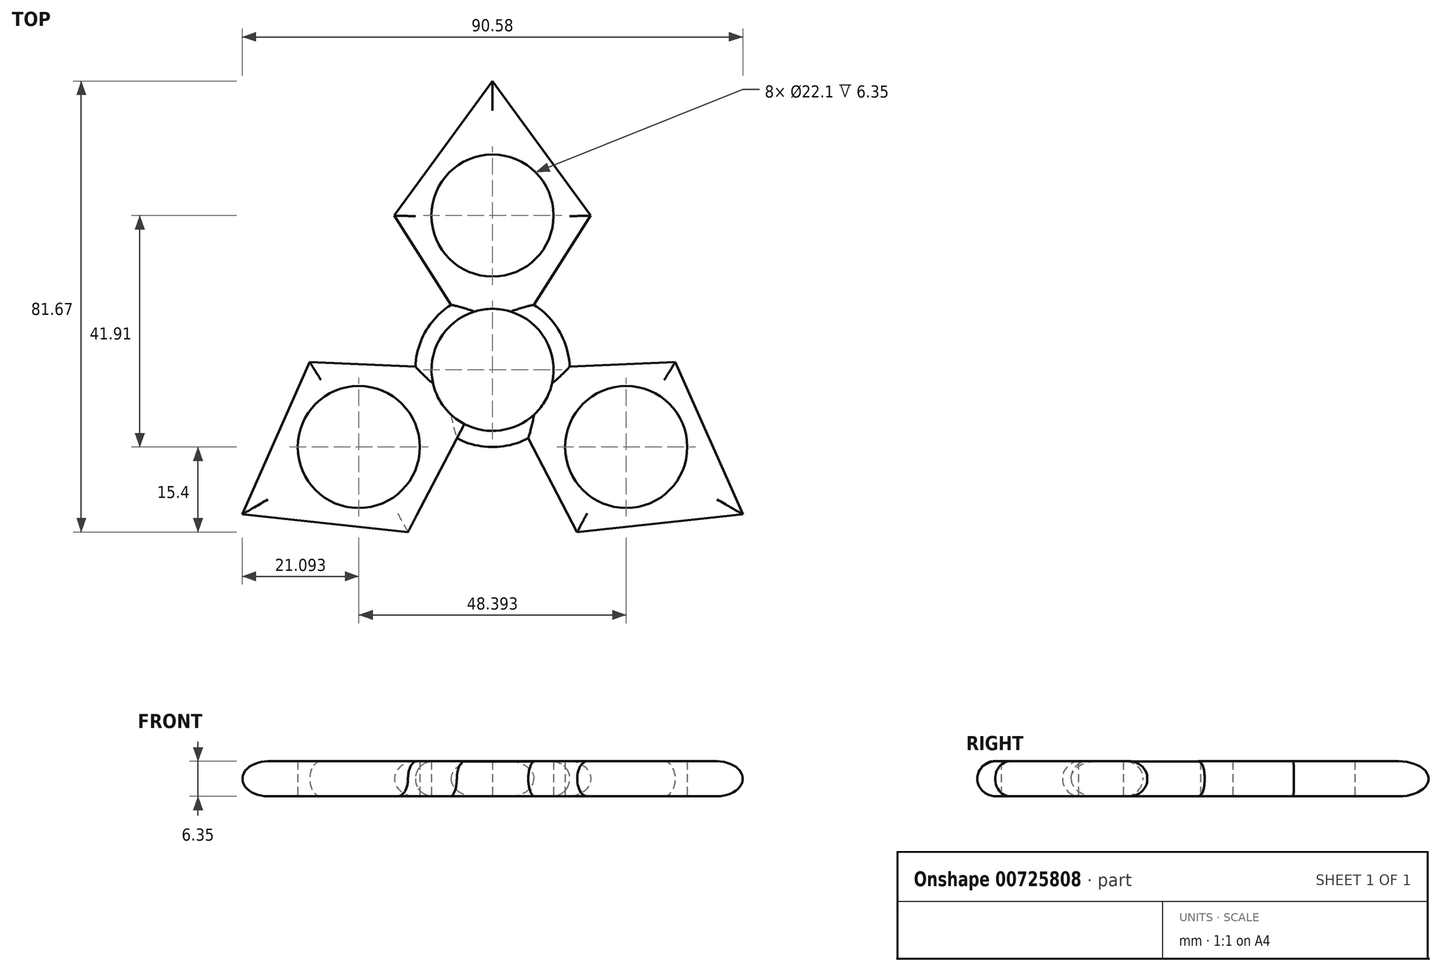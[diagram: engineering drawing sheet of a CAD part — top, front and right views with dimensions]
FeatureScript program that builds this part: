
annotation { "Feature Type Name" : "Feature", "Feature Type Description" : "" }
export const myFeature = defineFeature(function(context is Context, id is Id, definition is map)
    precondition{}
    {
        {
            var Q0;
            Q0=qCreatedBy(makeId("Top.planeOp"),FACE);
            var sketch = newSketch(context, id + "F0", { "sketchPlane" : qUnion([Q0])});
            skCircle(sketch, "E0", {"center": v(0, 0) * mm, "radius": 11.05 * mm});
            skCircle(sketch, "E1", {"center": v(0, 0) * mm, "radius": 13.97 * mm});
            skLineSegment(sketch, "E2", {"start": v(0, 0) * mm, "end": v(0, 27.94) * mm});
            skCircle(sketch, "E3", {"center": v(0, 27.94) * mm, "radius": 11.05 * mm});
            skCircle(sketch, "E4.1.0", {"center": v(-24.2, -13.97) * mm, "radius": 11.05 * mm});
            skCircle(sketch, "E4.2.0", {"center": v(24.2, -13.97) * mm, "radius": 11.05 * mm});
            skLineSegment(sketch, "E5", {"start": v(0, 27.94) * mm, "end": v(-17.78, 27.94) * mm});
            skLineSegment(sketch, "E6", {"start": v(0, 27.94) * mm, "end": v(17.78, 27.94) * mm});
            skLineSegment(sketch, "E7", {"start": v(-17.78, 27.94) * mm, "end": v(-7.5, 11.79) * mm});
            skLineSegment(sketch, "E8", {"start": v(17.78, 27.94) * mm, "end": v(7.5, 11.79) * mm});
            skLineSegment(sketch, "E9.1.2", {"start": v(-15.3, -29.37) * mm, "end": v(-6.46, -12.39) * mm});
            skLineSegment(sketch, "E9.1.3", {"start": v(-33.09, 1.43) * mm, "end": v(-13.96, 0.6) * mm});
            skLineSegment(sketch, "E9.2.2", {"start": v(33.09, 1.43) * mm, "end": v(13.96, 0.6) * mm});
            skLineSegment(sketch, "E9.2.3", {"start": v(15.3, -29.37) * mm, "end": v(6.46, -12.39) * mm});
            skLineSegment(sketch, "E10", {"start": v(-17.78, 27.94) * mm, "end": v(0, 52.3) * mm});
            skLineSegment(sketch, "E11", {"start": v(0, 52.3) * mm, "end": v(17.78, 27.94) * mm});
            skPoint(sketch, "E12.orphan", {"position": v(0, 48.26) * mm});
            skLineSegment(sketch, "E13.1.0", {"start": v(-15.3, -29.37) * mm, "end": v(-45.3, -26.15) * mm});
            skLineSegment(sketch, "E13.1.1", {"start": v(-45.3, -26.15) * mm, "end": v(-33.09, 1.43) * mm});
            skLineSegment(sketch, "E13.2.0", {"start": v(33.09, 1.43) * mm, "end": v(45.3, -26.15) * mm});
            skLineSegment(sketch, "E13.2.1", {"start": v(45.3, -26.15) * mm, "end": v(15.3, -29.37) * mm});
            skSolve(sketch);
        }
        {
            var Q0;
            Q0 = qSketchRegion(id + "F0", true);
            extrude(context, id + "F1", {"entities" : qUnion([Q0]), "depth" : 6.35 * mm, "offsetDistance" : 25.4 * mm});
        }
        {
            var Q0;
            Q0=makeQuery(id+"F1.opExtrude","CAP_EDGE",EDGE,{"disambiguationData":[OSD([sQuery(id+"F0.wireOp",EDGE,"E10")])],"isStart":false});
            var Q1;
            Q1=makeQuery(id+"F1.opExtrude","CAP_EDGE",EDGE,{"disambiguationData":[OSD([sQuery(id+"F0.wireOp",EDGE,"E11")])],"isStart":false});
            var Q2;
            Q2=makeQuery(id+"F1.opExtrude","CAP_EDGE",EDGE,{"disambiguationData":[OSD([sQuery(id+"F0.wireOp",EDGE,"E13.2.0")])],"isStart":false});
            var Q3;
            Q3=makeQuery(id+"F1.opExtrude","CAP_EDGE",EDGE,{"disambiguationData":[OSD([sQuery(id+"F0.wireOp",EDGE,"E13.2.1")])],"isStart":false});
            var Q4;
            Q4=makeQuery(id+"F1.opExtrude","CAP_EDGE",EDGE,{"disambiguationData":[OSD([sQuery(id+"F0.wireOp",EDGE,"E9.2.3")])],"isStart":false});
            var Q5;
            Q5=makeQuery(id+"F1.opExtrude","CAP_EDGE",EDGE,{"disambiguationData":[OSD([sQuery(id+"F0.wireOp",EDGE,"E9.2.2")])],"isStart":false});
            var Q6;
            {var subQ0=sQuery(id+"F0.wireOp",EDGE,"E1");Q6=makeQuery(id+"F1.opExtrude","CAP_EDGE",EDGE,{"disambiguationData":[OSD([subQ0]),TDD([makeQuery(id+"F0.imprint","IMPRINT",EDGE,{"disambiguationData":[TD([[makeQuery(id+"F0.imprint","INTERSECT",VERTEX,{"derivedFrom":[subQ0,sQuery(id+"F0.wireOp",EDGE,"E9.1.2")]}),-1.0]])],"derivedFrom":subQ0})])],"isStart":true});}
            var Q7;
            {var subQ0=sQuery(id+"F0.wireOp",EDGE,"E1");Q7=makeQuery(id+"F1.opExtrude","CAP_EDGE",EDGE,{"disambiguationData":[OSD([subQ0]),TDD([makeQuery(id+"F0.imprint","IMPRINT",EDGE,{"disambiguationData":[TD([[makeQuery(id+"F0.imprint","INTERSECT",VERTEX,{"derivedFrom":[subQ0,sQuery(id+"F0.wireOp",EDGE,"E8")]}),1.0]])],"derivedFrom":subQ0})])],"isStart":false});}
            var Q8;
            Q8=makeQuery(id+"F1.opExtrude","CAP_EDGE",EDGE,{"disambiguationData":[OSD([sQuery(id+"F0.wireOp",EDGE,"E8")])],"isStart":false});
            var Q9;
            Q9=makeQuery(id+"F1.opExtrude","CAP_EDGE",EDGE,{"disambiguationData":[OSD([sQuery(id+"F0.wireOp",EDGE,"E7")])],"isStart":false});
            var Q10;
            {var subQ0=sQuery(id+"F0.wireOp",EDGE,"E1");Q10=makeQuery(id+"F1.opExtrude","CAP_EDGE",EDGE,{"disambiguationData":[OSD([subQ0]),TDD([makeQuery(id+"F0.imprint","IMPRINT",EDGE,{"disambiguationData":[TD([[makeQuery(id+"F0.imprint","INTERSECT",VERTEX,{"derivedFrom":[subQ0,sQuery(id+"F0.wireOp",EDGE,"E7")]}),-1.0]])],"derivedFrom":subQ0})])],"isStart":false});}
            var Q11;
            Q11=makeQuery(id+"F1.opExtrude","CAP_EDGE",EDGE,{"disambiguationData":[OSD([sQuery(id+"F0.wireOp",EDGE,"E9.1.3")])],"isStart":false});
            var Q12;
            Q12=makeQuery(id+"F1.opExtrude","CAP_EDGE",EDGE,{"disambiguationData":[OSD([sQuery(id+"F0.wireOp",EDGE,"E13.1.1")])],"isStart":false});
            var Q13;
            Q13=makeQuery(id+"F1.opExtrude","CAP_EDGE",EDGE,{"disambiguationData":[OSD([sQuery(id+"F0.wireOp",EDGE,"E13.1.0")])],"isStart":true});
            var Q14;
            {var subQ0=sQuery(id+"F0.wireOp",EDGE,"E1");Q14=makeQuery(id+"F1.opExtrude","CAP_EDGE",EDGE,{"disambiguationData":[OSD([subQ0]),TDD([makeQuery(id+"F0.imprint","IMPRINT",EDGE,{"disambiguationData":[TD([[makeQuery(id+"F0.imprint","INTERSECT",VERTEX,{"derivedFrom":[subQ0,sQuery(id+"F0.wireOp",EDGE,"E9.1.2")]}),-1.0]])],"derivedFrom":subQ0})])],"isStart":false});}
            var Q15;
            Q15=makeQuery(id+"F1.opExtrude","CAP_EDGE",EDGE,{"disambiguationData":[OSD([sQuery(id+"F0.wireOp",EDGE,"E11")])],"isStart":true});
            var Q16;
            Q16=makeQuery(id+"F1.opExtrude","CAP_EDGE",EDGE,{"disambiguationData":[OSD([sQuery(id+"F0.wireOp",EDGE,"E10")])],"isStart":true});
            var Q17;
            Q17=makeQuery(id+"F1.opExtrude","CAP_EDGE",EDGE,{"disambiguationData":[OSD([sQuery(id+"F0.wireOp",EDGE,"E7")])],"isStart":true});
            var Q18;
            Q18=makeQuery(id+"F1.opExtrude","CAP_EDGE",EDGE,{"disambiguationData":[OSD([sQuery(id+"F0.wireOp",EDGE,"E8")])],"isStart":true});
            var Q19;
            {var subQ0=sQuery(id+"F0.wireOp",EDGE,"E1");Q19=makeQuery(id+"F1.opExtrude","CAP_EDGE",EDGE,{"disambiguationData":[OSD([subQ0]),TDD([makeQuery(id+"F0.imprint","IMPRINT",EDGE,{"disambiguationData":[TD([[makeQuery(id+"F0.imprint","INTERSECT",VERTEX,{"derivedFrom":[subQ0,sQuery(id+"F0.wireOp",EDGE,"E8")]}),1.0]])],"derivedFrom":subQ0})])],"isStart":true});}
            var Q20;
            Q20=makeQuery(id+"F1.opExtrude","CAP_EDGE",EDGE,{"disambiguationData":[OSD([sQuery(id+"F0.wireOp",EDGE,"E9.2.2")])],"isStart":true});
            var Q21;
            Q21=makeQuery(id+"F1.opExtrude","CAP_EDGE",EDGE,{"disambiguationData":[OSD([sQuery(id+"F0.wireOp",EDGE,"E13.2.0")])],"isStart":true});
            var Q22;
            Q22=makeQuery(id+"F1.opExtrude","CAP_EDGE",EDGE,{"disambiguationData":[OSD([sQuery(id+"F0.wireOp",EDGE,"E13.2.1")])],"isStart":true});
            var Q23;
            Q23=makeQuery(id+"F1.opExtrude","CAP_EDGE",EDGE,{"disambiguationData":[OSD([sQuery(id+"F0.wireOp",EDGE,"E9.2.3")])],"isStart":true});
            var Q24;
            {var subQ0=sQuery(id+"F0.wireOp",EDGE,"E1");Q24=makeQuery(id+"F1.opExtrude","CAP_EDGE",EDGE,{"disambiguationData":[OSD([subQ0]),TDD([makeQuery(id+"F0.imprint","IMPRINT",EDGE,{"disambiguationData":[TD([[makeQuery(id+"F0.imprint","INTERSECT",VERTEX,{"derivedFrom":[subQ0,sQuery(id+"F0.wireOp",EDGE,"E7")]}),-1.0]])],"derivedFrom":subQ0})])],"isStart":true});}
            var Q25;
            Q25=makeQuery(id+"F1.opExtrude","CAP_EDGE",EDGE,{"disambiguationData":[OSD([sQuery(id+"F0.wireOp",EDGE,"E9.1.2")])],"isStart":true});
            var Q26;
            Q26=makeQuery(id+"F1.opExtrude","CAP_EDGE",EDGE,{"disambiguationData":[OSD([sQuery(id+"F0.wireOp",EDGE,"E9.1.3")])],"isStart":true});
            var Q27;
            Q27=makeQuery(id+"F1.opExtrude","CAP_EDGE",EDGE,{"disambiguationData":[OSD([sQuery(id+"F0.wireOp",EDGE,"E13.1.1")])],"isStart":true});
            var Q28;
            Q28=makeQuery(id+"F1.opExtrude","CAP_EDGE",EDGE,{"disambiguationData":[OSD([sQuery(id+"F0.wireOp",EDGE,"E13.1.0")])],"isStart":false});
            fillet(context, id + "F2", {"entities" : qUnion([Q0, Q1, Q2, Q3, Q4, Q5, Q6, Q7, Q8, Q9, Q10, Q11, Q12, Q13, Q14, Q15, Q16, Q17, Q18, Q19, Q20, Q21, Q22, Q23, Q24, Q25, Q26, Q27, Q28]), "radius" : 3.17 * mm, "tangentPropagation" : true, "allowEdgeOverflow" : false});
        }
    });
